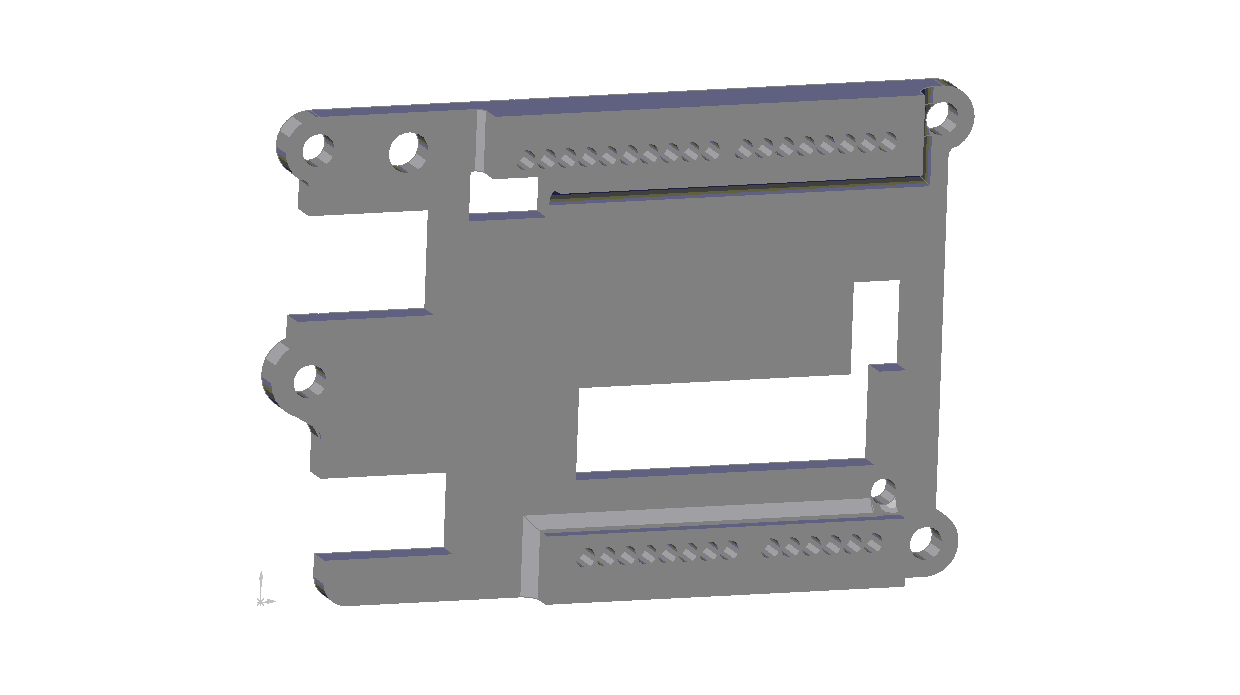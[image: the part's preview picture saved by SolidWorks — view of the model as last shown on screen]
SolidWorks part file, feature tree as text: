
SOLIDWORKS PART (.sldprt)
format: sldprt  version: not decoded by parser v0  size: 877,568 bytes
history: native  units: mm
features: fillet x5, plane x3, sketch x3, extrude x3, material x1 (+10 scaffold rows collapsed)
feature tree (25):
  scaffold x10  (default folders/planes/origin — collapsed)
  material  "Matériau <non spécifié>"
  plane  "Plan de face"
  plane  "Plan de dessus"
  plane  "Plan de droite"
  sketch  "Esquisse1"  dims[D1=3.2mm D6=5.0mm D2=6.5mm D3=10.5mm D4=7.0mm D5=4.0mm]
  extrude  "Extrusion1"  Depth=2.8mm
  sketch  "Esquisse2"  dims[D1=1.0mm D2=1.0mm D3=1.0mm D4=1.0mm D5=1.0mm D6=1.0mm D7=1.0mm D8=1.0mm D9=1.0mm D10=1.0mm D11=1.0mm D12=1.0mm D13=1.0mm D14=1.0mm D15=1.0mm D16=1.0mm D17=1.0mm D18=1.0mm D19=1.0mm D20=1.0mm D21=1.0mm D22=1.0mm D23=1.0mm D24=1.0mm D25=1.0mm D26=1.0mm D27=1.0mm D28=1.0mm D29=1.0mm D30=1.0mm D31=1.0mm D32=1.0mm]
  extrude  "Extrusion2"  Depth=0.8mm
  sketch  "Esquisse3"  dims[D1=2.5mm D2=2.5mm D3=2.5mm D4=2.5mm D5=2.5mm D6=2.5mm D7=2.5mm D8=2.5mm D9=2.5mm D10=2.5mm D11=2.5mm D12=2.5mm D13=2.5mm D14=2.5mm D15=2.5mm D16=2.5mm D17=2.5mm D18=2.5mm D19=2.5mm D20=2.5mm D21=2.5mm D22=2.5mm D23=2.5mm D24=2.5mm D25=2.5mm D26=2.5mm D27=2.5mm D28=2.5mm D29=2.5mm D30=2.5mm D31=2.5mm D32=2.5mm]
  extrude  "Extrusion3"  Depth=4mm
  fillet  "Congé1"  Radius=3mm
  fillet  "Congé2"  Radius=3mm
  fillet  "Congé7"  Radius=1mm
  fillet  "Congé9"  Radius=2mm
  fillet  "Congé10"  Radius=2mm
decode coverage: 11 of 11 modeling features carry decoded parameters
note: suppression state not decoded; provenance and decode notes live in map.json
